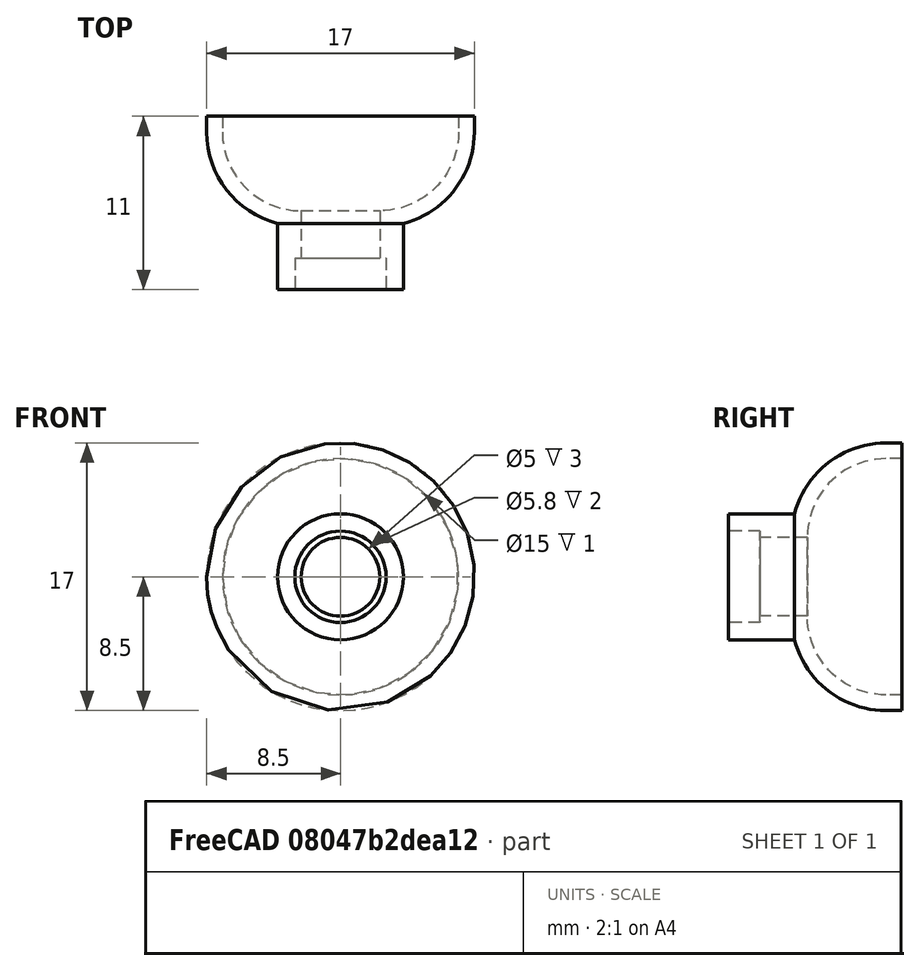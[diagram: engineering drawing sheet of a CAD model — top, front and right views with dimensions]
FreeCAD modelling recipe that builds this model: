
FCSTD DOCUMENT
Label: LEDLightBucket
objects: Sketcher::SketchObject×1, Part::Revolution×1
note: 2 computed .brp shape members not serialized (recipe doc carries the construction recipe); baked Part::Feature solids carry a one-line shape summary decoded from their .brp

FEATURE [Sketcher::SketchObject] Sketch
  sketch-geometry (10):
    g0: LineSegment StartX=-2.5 StartY=5 StartZ=0 EndX=-2.5 EndY=2 EndZ=0
    g1: LineSegment StartX=-4 StartY=0 StartZ=0 EndX=-4 EndY=4.19052 EndZ=0
    g2: LineSegment StartX=-2.5 StartY=2 StartZ=0 EndX=-2.9 EndY=2 EndZ=0
    g3: LineSegment StartX=-2.9 StartY=2 StartZ=0 EndX=-2.9 EndY=0 EndZ=0
    g4: LineSegment StartX=-2.9 StartY=0 StartZ=0 EndX=-4 EndY=0 EndZ=0
    g5: LineSegment StartX=-8.5 StartY=10 StartZ=0 EndX=-8.5 EndY=11 EndZ=0
    g6: LineSegment StartX=-8.5 StartY=11 StartZ=0 EndX=-7.5 EndY=11 EndZ=0
    g7: LineSegment StartX=-7.5 StartY=11 StartZ=0 EndX=-7.5 EndY=10 EndZ=0
    g8: ArcOfCircle CenterX=-2.5 CenterY=10 CenterZ=0 NormalX=0 NormalY=0 NormalZ=1 Radius=6 StartAngle=3.14159 EndAngle=4.45971
    g9: ArcOfCircle CenterX=-2.5 CenterY=10 CenterZ=0 NormalX=0 NormalY=0 NormalZ=1 Radius=5 StartAngle=3.14159 EndAngle=4.71239
  constraints (31):
    c: Vertical(g0)
    c: Vertical(g1)
    c: Coincident(g2,g3)
    c: Coincident(g3,g4)
    c: Horizontal(g4)
    c: Horizontal(g2)
    c: Vertical(g3)
    c: Coincident(g4,g1)
    c: Coincident(g2,g0)
    c: Distance(g3) = 2
    c: Distance(g4) = 1.1
    c: Distance(g0) = 3
    c: DistanceX(g3) = -2.9
    c: DistanceY(g3) = 0
    c: Coincident(g5,g6)
    c: Vertical(g7)
    c: Horizontal(g6)
    c: Vertical(g5)
    c: Distance(g5) = 1
    c: Coincident(g7,g6)
    c: Distance(g6) = 1
    c: Coincident(g8,g1)
    c: Coincident(g8,g5)
    c: Coincident(g9,g0)
    c: Coincident(g9,g7)
    c: Coincident(g9,g8)
    c: Radius(g8) = 6
    c: Tangent(g8,g5)
    c: Tangent(g7,g9)
    c: Distance(g2) = 0.4
    c: DistanceX(g8) = -2.5
FEATURE [Part::Revolution] Revolve
  Angle = 360
  Axis = (0,1,0)
  Base = (0,0,0)
  Source = -> Sketch
